# Revit family: Lighting-Luminii-Bara_Static_White
name_source: partatom
category: Lighting Fixtures
units: mm (PartAtom-declared; Revit-internal decimal feet)

## family parameters
Cut with Voids When Loaded = No
Host = Face
Light Source = Yes
OmniClass Number = 23.80.70.11.14.21
OmniClass Title = Spots and Tracklight Specialties
Part Type = Normal
Room Calculation Point = No
Round Connector Dimension = Use Diameter
Shared = Yes

## types (8) — shared parameters
Assembly Code = D5020230
C End Caps Width = 0.06 "
CCT = 3000K
Color Filter = 16777215
Current Amps = 50 A
Description = Linear Illumination System
Dimming Lamp Color Temperature Shift = <None>
Emit Shape Visible in Rendering = No
Emit from Rectangle Length = 48 "
Emit from Rectangle Width = 0.06 "
Environment = Indoor
Finish = Metal - Luminii - Silver Anodized Aluminum
Frequency = 60 Hz
Has Battery Backup = No
Has Dimming = Yes
Housing Protection Rating = IP20 Dry/IP66 Wet Series
Initial Color Comments = Perfomance based on 3500K Photometric Web File
Keynote = 26 50 00
Lamp = LED
Lamp Life = 1
Lens Material = Plastic - Luminii - Frosted Lens
Load Classification = Lighting
Manufacturer = Luminii
Mounting Method = Surface Mount
Number of Poles = 1
Operating Temperature = Consult Manufacturer Website for more Information
Phase = 1
Power Factor = 1
Power Source Type = Driver
Product Page URL = https://www.luminii.com
URL = https://www.luminii.com
Version = 2020 - v1.0a
Voltage = 120 V
Voltage Comments = 120VAC - 277VAC
Warranty URL = https://www.luminii.com
Width = 0.93 "
zero-valued in all types: C Offset From Face, Default Elevation

## per-type parameters (varying)
| type | Apparent Load | Asymmetric | Batwing | Constraints | Depth | Frosted Lens | High Color Quality | High Efficacy | Lumen Output | Model | Narrow Beam | Photometric Web File | Tilt Angle | Wattage Comments | not Asymmetric |
| Bara Static White - High Color Quality - Frosted | 3 VA | No | No | 1 | 0.41 " | Yes | Yes | No | 159 lm/ft | Bara-72XX | No | BAR-48-30K-LL72VHO-F.IES | 60.00° | 2.8 W/ft | Yes |
| Bara Static White - High Efficacy - Frosted | 2 VA | No | No | 1 | 0.41 " | Yes | No | Yes | 155 lm/ft | Bara-HEXXXX | No | BAR-48-30K-LL72VHO-F.IES | 90.00° | 1.9 W/ft | Yes |
| Bara Static White - High Efficacy - Narrow Beam | 2 VA | No | No | 2 | 0.41 " | No | No | Yes | 155 lm/ft | Bara-HEXXXX | Yes | Narrow Beam LL72-VHO-30K_IESNA2002.ies | 60.00° | 1.9 W/ft | Yes |
| Bara Static White - High Color Quality - Narrow Beam | 3 VA | No | No | 2 | 0.41 " | No | Yes | No | 159 lm/ft | Bara-72XX | Yes | Narrow Beam LL72-VHO-30K_IESNA2002.ies | 60.00° | 2.8 W/ft | Yes |
| Bara Static White - High Efficacy - Batwing | 2 VA | No | Yes | 3 | 0.41 " | No | No | Yes | 155 lm/ft | Bara-HEXXXX | No | Batwing Bara LL72-VHO-30K_IESNA2002.ies | 60.00° | 1.9 W/ft | Yes |
| Bara Static White - High Color Quality - Batwing | 3 VA | No | Yes | 3 | 0.41 " | No | Yes | No | 159 lm/ft | Bara-72XX | No | Batwing Bara LL72-VHO-30K_IESNA2002.ies | 60.00° | 2.8 W/ft | Yes |
| Bara Static White - High Color Quality - Asymmetric | 3 VA | Yes | No | 4 | 0.5 " | No | Yes | No | 159 lm/ft | Bara-72XX | No | Asymmetric Lens Bara LL72-VHO-30K_IESNA2002.ies | 60.00° | 2.8 W/ft | No |
| Bara Static White - High Efficacy - Asymmetric | 2 VA | Yes | No | 4 | 0.5 " | No | No | Yes | 155 lm/ft | Bara-HEXXXX | No | Asymmetric Lens Bara LL72-VHO-30K_IESNA2002.ies | 90.00° | 1.9 W/ft | No |

## geometry (parser evidence)
native form markers: Sweep x7
no freeform markers — native parametric forms only
